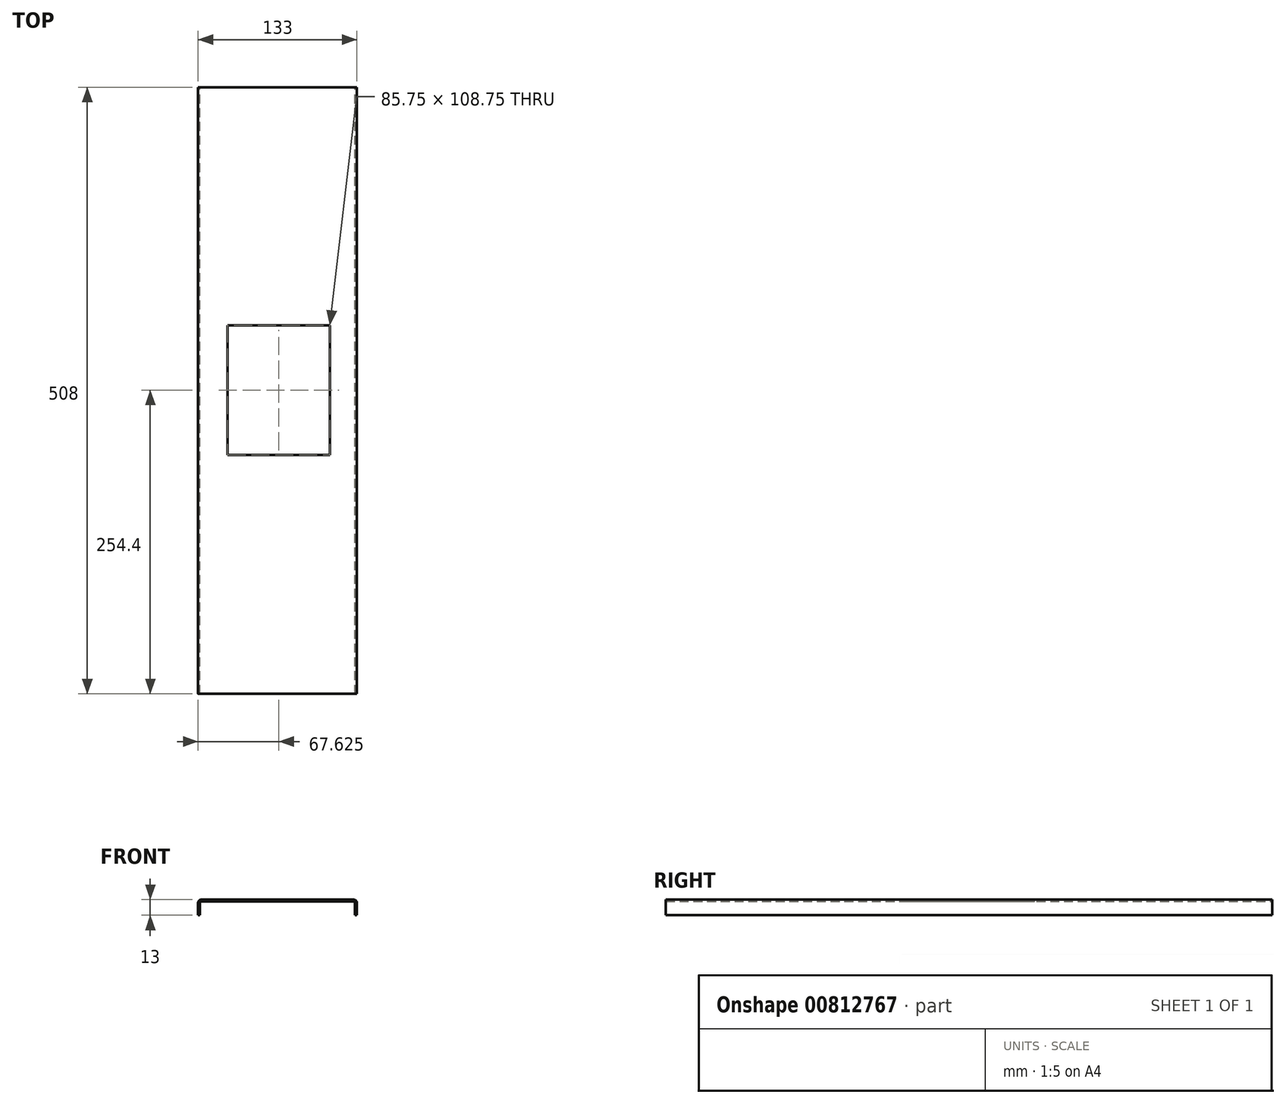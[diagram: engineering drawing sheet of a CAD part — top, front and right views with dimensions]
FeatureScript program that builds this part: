
annotation { "Feature Type Name" : "Feature", "Feature Type Description" : "" }
export const myFeature = defineFeature(function(context is Context, id is Id, definition is map)
    precondition{}
    {
        {
            var Q0;
            Q0=qCreatedBy(makeId("Front.planeOp"),FACE);
            var sketch = newSketch(context, id + "F0", { "sketchPlane" : qUnion([Q0])});
            skLineSegment(sketch, "E0", {"start": v(0, 0) * mm, "end": v(0, 10.5) * mm});
            skLineSegment(sketch, "E1", {"start": v(2.5, 13) * mm, "end": v(130.5, 13) * mm});
            skLineSegment(sketch, "E2", {"start": v(133, 10.5) * mm, "end": v(133, 0) * mm});
            skLineSegment(sketch, "E3", {"start": v(133, 0) * mm, "end": v(131.5, 0) * mm});
            skLineSegment(sketch, "E4", {"start": v(131.5, 0) * mm, "end": v(131.5, 11.5) * mm});
            skLineSegment(sketch, "E5", {"start": v(131.5, 11.5) * mm, "end": v(1.5, 11.5) * mm});
            skLineSegment(sketch, "E6", {"start": v(1.5, 11.5) * mm, "end": v(1.5, 0) * mm});
            skLineSegment(sketch, "E7", {"start": v(1.5, 0) * mm, "end": v(0, 0) * mm});
            skPoint(sketch, "E8.visualSharp", {"position": v(133, 13) * mm});
            skArc(sketch, "E8.filletArc", {"start": v(133, 10.5) * mm, "mid": v(132.27, 12.27) * mm, "end": v(130.5, 13) * mm});
            skPoint(sketch, "E9.visualSharp", {"position": v(0, 13) * mm});
            skArc(sketch, "E9.filletArc", {"start": v(2.5, 13) * mm, "mid": v(0.73, 12.27) * mm, "end": v(0, 10.5) * mm});
            skSolve(sketch);
        }
        {
            var Q0;
            Q0=makeQuery(id+"F0.imprint","IMPRINT",FACE,{"disambiguationData":[TD([[makeQuery(id+"F0.imprint","IMPRINT",EDGE,{"derivedFrom":sQuery(id+"F0.wireOp",EDGE,"E0")}),-1.0]])]});
            extrude(context, id + "F1", {"entities" : qUnion([Q0]), "depth" : 508 * mm, "offsetDistance" : 25 * mm});
        }
        {
            var Q0;
            Q0=makeQuery(id+"F1.opExtrude","SWEPT_FACE",FACE,{"disambiguationData":[OSD([sQuery(id+"F0.wireOp",EDGE,"E1")])]});
            var sketch = newSketch(context, id + "F2", { "sketchPlane" : qUnion([Q0])});
            skLineSegment(sketch, "E10.bottom", {"start": v(24.75, -199.22) * mm, "end": v(110.5, -199.22) * mm});
            skLineSegment(sketch, "E10.top", {"start": v(24.75, -307.98) * mm, "end": v(110.5, -307.98) * mm});
            skLineSegment(sketch, "E10.left", {"start": v(24.75, -199.22) * mm, "end": v(24.75, -307.98) * mm});
            skLineSegment(sketch, "E10.right", {"start": v(110.5, -199.22) * mm, "end": v(110.5, -307.98) * mm});
            skSolve(sketch);
        }
        {
            var Q0;
            Q0 = qSketchRegion(id + "F2", true);
            extrude(context, id + "F3", {"entities" : qUnion([Q0]), "operationType" : NewBodyOperationType.REMOVE, "oppositeDirection" : true, "depth" : 25 * mm, "offsetDistance" : 25 * mm});
        }
    });
